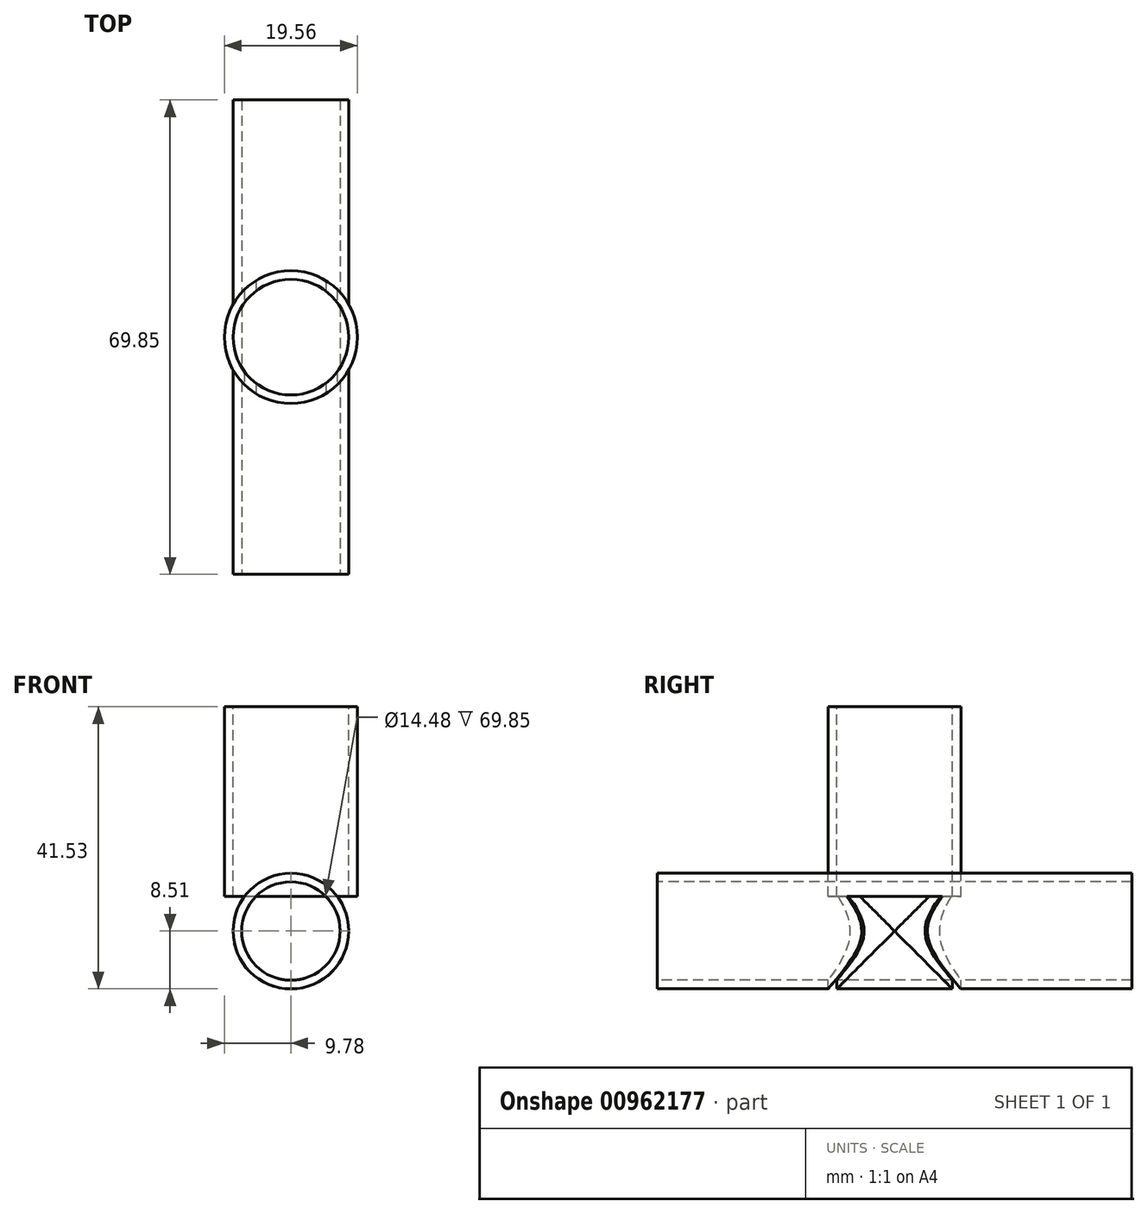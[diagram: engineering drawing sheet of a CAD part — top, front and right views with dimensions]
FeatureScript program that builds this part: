
annotation { "Feature Type Name" : "Feature", "Feature Type Description" : "" }
export const myFeature = defineFeature(function(context is Context, id is Id, definition is map)
    precondition{}
    {
        {
            var Q0;
            Q0=qCreatedBy(makeId("Front.planeOp"),FACE);
            var sketch = newSketch(context, id + "F0", { "sketchPlane" : qUnion([Q0])});
            skCircle(sketch, "E0", {"center": v(0, 0) * mm, "radius": 7.24 * mm});
            skCircle(sketch, "E1", {"center": v(0, 0) * mm, "radius": 8.5 * mm});
            skSolve(sketch);
        }
        {
            var Q0;
            Q0=qCreatedBy(makeId("Right.planeOp"),FACE);
            var sketch = newSketch(context, id + "F1", { "sketchPlane" : qUnion([Q0])});
            skLineSegment(sketch, "E2", {"start": v(0, 0) * mm, "end": v(-69.85, 0) * mm});
            skSolve(sketch);
        }
        {
            var Q0;
            Q0=makeQuery(id+"F0.imprint","IMPRINT",FACE,{"disambiguationData":[TD([[makeQuery(id+"F0.imprint","IMPRINT",EDGE,{"derivedFrom":sQuery(id+"F0.wireOp",EDGE,"E0")}),-1.0]])]});
            var Q1;
            Q1 = qSketchRegion(id + "FB4Myxkzfn3SVVL_1", true);
            var Q2;
            Q2=sQuery(id+"F1.wireOp",EDGE,"E2");
            sweep(context, id + "F2", {"profiles" : qUnion([Q0, Q1]), "path" : qUnion([Q2])});
        }
        {
            var Q0;
            Q0=qCreatedBy(makeId("Top.planeOp"),FACE);
            var sketch = newSketch(context, id + "F3", { "sketchPlane" : qUnion([Q0])});
            skCircle(sketch, "E3", {"center": v(0, -34.93) * mm, "radius": 9.78 * mm});
            skCircle(sketch, "E4", {"center": v(0, -34.93) * mm, "radius": 8.5 * mm});
            skSolve(sketch);
        }
        {
            var Q0;
            Q0=qCreatedBy(makeId("Right.planeOp"),FACE);
            var sketch = newSketch(context, id + "F4", { "sketchPlane" : qUnion([Q0])});
            skLineSegment(sketch, "E5", {"start": v(-34.93, 0) * mm, "end": v(-34.93, 38.1) * mm});
            skSolve(sketch);
        }
        {
            var Q0;
            Q0=makeQuery(id+"F3.imprint","IMPRINT",FACE,{"disambiguationData":[TD([[makeQuery(id+"F3.imprint","IMPRINT",EDGE,{"derivedFrom":sQuery(id+"F3.wireOp",EDGE,"E3")}),1.0]])]});
            var Q1;
            Q1=sQuery(id+"F4.wireOp",EDGE,"E5");
            sweep(context, id + "F5", {"profiles" : qUnion([Q0]), "path" : qUnion([Q1])});
        }
        {
            var Q0;
            Q0=makeQuery(id+"F5.opSweep","CAP_FACE",FACE,{"disambiguationData":[OSD([sQuery(id+"F3.wireOp",EDGE,"E3"),sQuery(id+"F3.wireOp",EDGE,"E4"),sQuery(id+"F4.wireOp",VERTEX,"E5.start")])],"isStart":true});
            extrude(context, id + "F6", {"entities" : qUnion([Q0]), "operationType" : NewBodyOperationType.REMOVE, "depth" : 20.83 * mm, "offsetDistance" : 25.4 * mm, "hasSecondDirection" : true, "secondDirectionOppositeDirection" : true, "secondDirectionDepth" : 5.08 * mm});
        }
        {
            var Q0;
            Q0=makeQuery(id+"F5.opSweep","CAP_FACE",FACE,{"disambiguationData":[OSD([sQuery(id+"F3.wireOp",EDGE,"E3"),sQuery(id+"F3.wireOp",EDGE,"E4"),sQuery(id+"F4.wireOp",VERTEX,"E5.end")])],"isStart":false});
            extrude(context, id + "F7", {"entities" : qUnion([Q0]), "operationType" : NewBodyOperationType.REMOVE, "oppositeDirection" : true, "depth" : 5.08 * mm, "offsetDistance" : 25.4 * mm});
        }
    });
